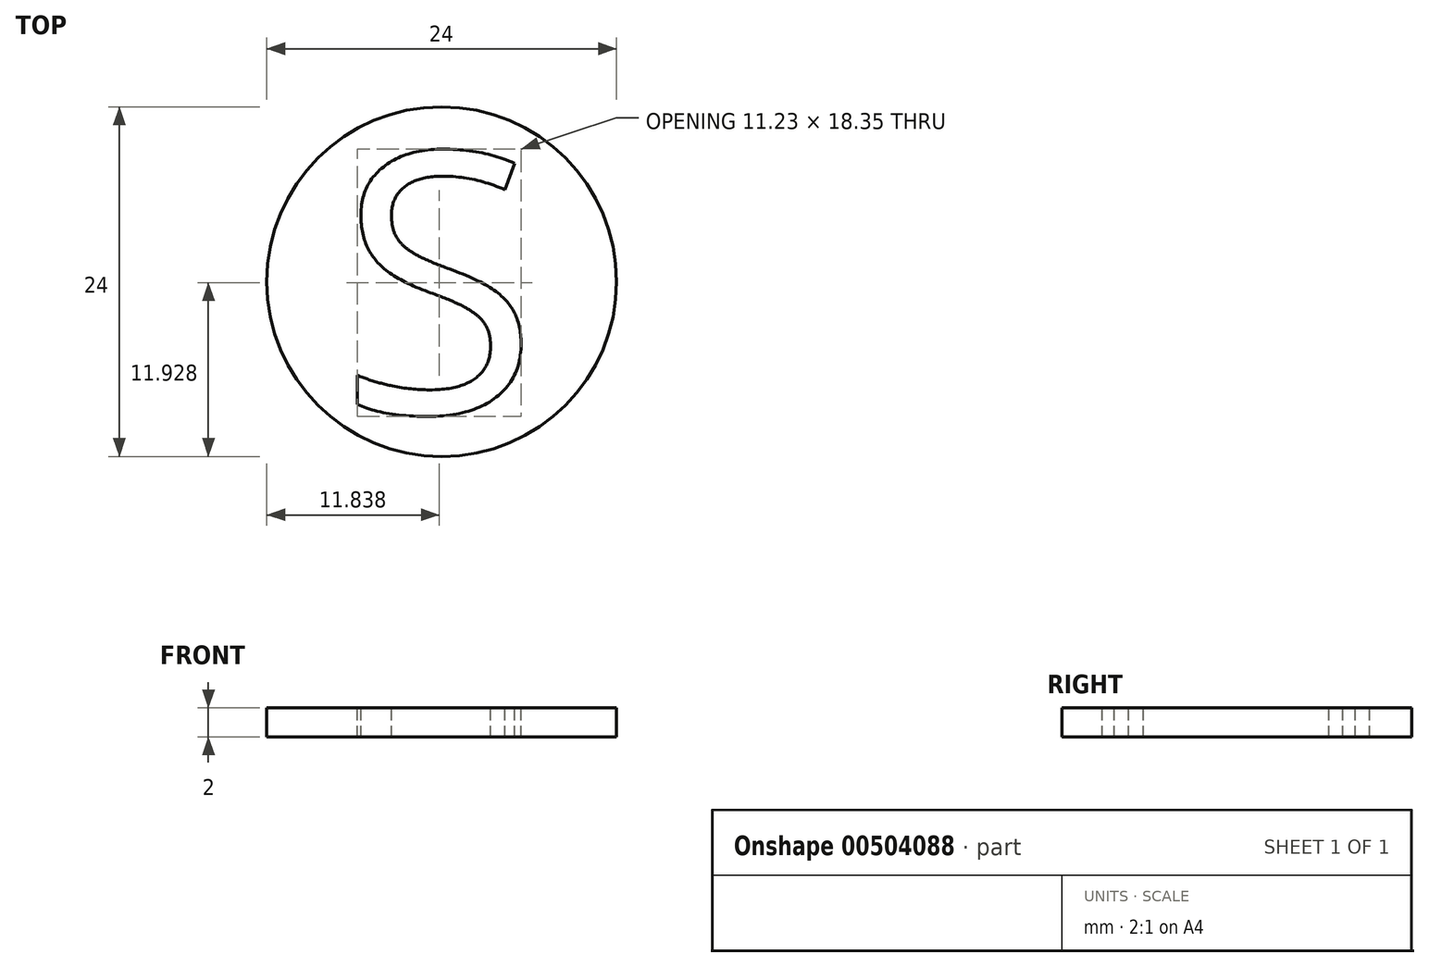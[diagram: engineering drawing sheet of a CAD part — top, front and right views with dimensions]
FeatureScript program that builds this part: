
annotation { "Feature Type Name" : "Feature", "Feature Type Description" : "" }
export const myFeature = defineFeature(function(context is Context, id is Id, definition is map)
    precondition{}
    {
        {
            var Q0;
            Q0=qCreatedBy(makeId("Top.planeOp"),FACE);
            var sketch = newSketch(context, id + "F0", { "sketchPlane" : qUnion([Q0])});
            skCircle(sketch, "E0", {"center": v(0, 0) * mm, "radius": 12 * mm});
            skSolve(sketch);
        }
        {
            var Q0;
            Q0=qSketchRegion(id+"F0",true);
            extrude(context, id + "F1", {"entities" : qUnion([Q0]), "depth" : 2 * mm});
        }
        {
            var Q0;
            Q0=makeQuery(id+"F1.opExtrude","CAP_FACE",FACE,{"disambiguationData":[OSD([sQuery(id+"F0.wireOp",EDGE,"E0")])],"isStart":false});
            var sketch = newSketch(context, id + "F2", { "sketchPlane" : qUnion([Q0])});
            skText(sketch, "E1", { "text": "S", "fontName": "OpenSans-Regular.ttf"});
            skPoint(sketch, "E2", {"position": v(7.07, 0) * mm});
            const initialGuessF2  = {"E1": [-0.00707, -0.009, 1, 0, 0.018]};
            skSetInitialGuess(sketch, initialGuessF2);
            skSolve(sketch);
        }
        {
            var Q0;
            Q0 = qSketchRegion(id + "F2", true);
            extrude(context, id + "F3", {"entities" : qUnion([Q0]), "operationType" : NewBodyOperationType.REMOVE, "oppositeDirection" : true, "depth" : 25 * mm, "offsetDistance" : 25 * mm});
        }
    });
